# Revit family: P191568KX-083c_KOCE500E
name_source: partatom
category: Specialty Equipment
units: mm (PartAtom-declared; Revit-internal decimal feet)

## family parameters
Always vertical = Yes
Cut with Voids When Loaded = No
Enable Cutting in Views = No
Maintain Annotation Orientation = No
Part Type = Normal
Room Calculation Point = No
Round Connector Dimension = Use Diameter
Shared = No
Work Plane-Based = No

## types (1)
- KOCE500ESS
    Amps = 40 A
    Body Material = ARCAT - Metal - Steel - Stainless
    Clearance Material = ARCAT - Clearance
    Default Elevation = 0"
    Depth = 27 1/8"
    Description = 30" Combination Wall Oven with Even-Heat™  True Convection (Lower Oven)
Four mural combiné à convection véritable EvenHeat™ (four inférieur), 30 po
    Dimension Guide = http://access.whirlpool.com Guide&sku=KOCE500EBL&language=EN
http://access.whirlpool.com Guide&sku=KOCE500EBL&language=EN
    Display Panel Material = ARCAT - Glass - Black
    Door Material = ARCAT - Metal - Steel - Stainless
    Family Name = COOKING
    Feature 1 = Even-Heat™ True Convection Oven (lower oven)
Four à convection véritable Even-Heat™ (four inférieur)
    Feature 2 = Microwave Convection Cooking (upper oven)
Cuisson au four à micro-ondes à convection (four supérieur)
    Feature 3 = Professionally-Inspired Design
Conception d'inspiration professionnelle (éclairage des commandes- blanc)
    Glass Material = ARCAT - Glass - Tempered - Black
    Handle Material = ARCAT - Metal - Steel - Gray
    Height = 42 1/2"
    Installation-Fabrication = http://access.whirlpool.com Instruction&sku=KOCE500EBL&language=EN
http://access.whirlpool.com Instruction&sku=KOCE500EBL&language=FR
    Manufacturer = Kitchen Aid
    Model = KOCE500ESS
    Voltage = 0 V
    Width = 30"

## geometry (parser evidence)
native form markers: Sweep x6
no freeform markers — native parametric forms only
